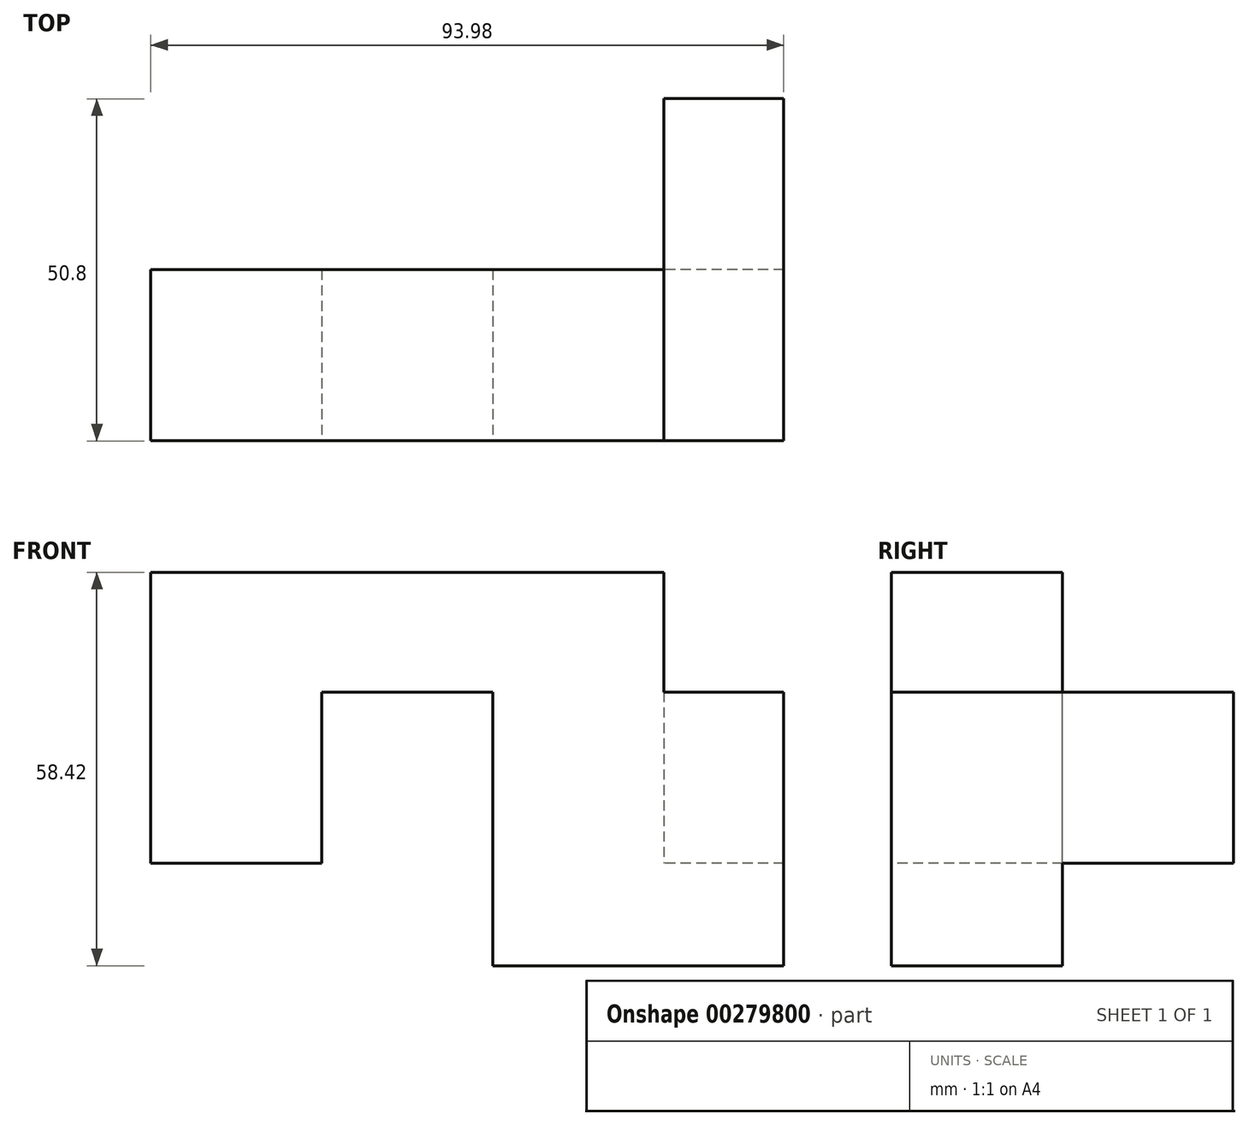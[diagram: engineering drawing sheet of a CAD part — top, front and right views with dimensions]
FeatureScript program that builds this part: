
annotation { "Feature Type Name" : "Feature", "Feature Type Description" : "" }
export const myFeature = defineFeature(function(context is Context, id is Id, definition is map)
    precondition{}
    {
        {
            var Q0;
            Q0=qCreatedBy(makeId("Right.planeOp"),FACE);
            var sketch = newSketch(context, id + "F0", { "sketchPlane" : qUnion([Q0])});
            skLineSegment(sketch, "E0.bottom", {"start": v(27.06, 34.15) * mm, "end": v(52.46, 34.15) * mm});
            skLineSegment(sketch, "E0.top", {"start": v(27.06, 8.75) * mm, "end": v(52.46, 8.75) * mm});
            skLineSegment(sketch, "E0.left", {"start": v(27.06, 34.15) * mm, "end": v(27.06, 8.75) * mm});
            skLineSegment(sketch, "E0.right", {"start": v(52.46, 34.15) * mm, "end": v(52.46, 8.75) * mm});
            skSolve(sketch);
        }
        {
            var Q0;
            Q0=makeQuery(id+"F0.imprint","IMPRINT",FACE,{"disambiguationData":[TD([[makeQuery(id+"F0.imprint","IMPRINT",EDGE,{"derivedFrom":sQuery(id+"F0.wireOp",EDGE,"E0.bottom")}),-1.0]])]});
            extrude(context, id + "F1", {"entities" : qUnion([Q0]), "depth" : 17.78 * mm});
        }
        {
            var Q0;
            Q0=makeQuery(id+"F1.opExtrude","SWEPT_FACE",FACE,{"disambiguationData":[OSD([sQuery(id+"F0.wireOp",EDGE,"E0.left")])]});
            extrude(context, id + "F2", {"entities" : qUnion([Q0]), "operationType" : NewBodyOperationType.ADD, "depth" : 25.4 * mm});
        }
        {
            var Q0;
            {var subQ0=sQuery(id+"F0.wireOp",EDGE,"E0.top");Q0=makeQuery(id+"F2.boolean.opBoolean","MERGE",FACE,{"derivedFrom":[makeQuery(id+"F1.opExtrude","SWEPT_FACE",FACE,{"disambiguationData":[OSD([subQ0])]}),makeQuery(id+"F2.opExtrude","SWEPT_FACE",FACE,{"disambiguationData":[OSD([subQ0,sQuery(id+"F0.wireOp",EDGE,"E0.left")])]})]});}
            var sketch = newSketch(context, id + "F3", { "sketchPlane" : qUnion([Q0])});
            skLineSegment(sketch, "E1", {"start": v(17.78, -27.06) * mm, "end": v(0, -27.06) * mm});
            skSolve(sketch);
        }
        {
            var Q0;
            {var subQ0=sQuery(id+"F3.wireOp",EDGE,"E1");Q0=makeQuery(id+"F3.imprint","IMPRINT",FACE,{"disambiguationData":[TD([[makeQuery(id+"F3.imprint","IMPRINT",EDGE,{"derivedFrom":subQ0}),-1.0]])]});}
            extrude(context, id + "F4", {"entities" : qUnion([Q0]), "operationType" : NewBodyOperationType.ADD, "depth" : 15.24 * mm});
        }
        {
            var Q0;
            {var subQ0=sQuery(id+"F0.wireOp",EDGE,"E0.left");var subQ1=sQuery(id+"F0.wireOp",EDGE,"E0.top");var subQ2=makeQuery(id+"F2.boolean.opBoolean","MERGE",EDGE,{"derivedFrom":[makeQuery(id+"F1.opExtrude","CAP_EDGE",EDGE,{"disambiguationData":[OSD([subQ1])],"isStart":true}),makeQuery(id+"F2.opExtrude","SWEPT_EDGE",EDGE,{"disambiguationData":[OSD([subQ1,subQ0]),TDD([makeQuery(id+"F1.opExtrude","CAP_VERTEX",VERTEX,{"disambiguationData":[OSD([subQ1,subQ0])],"isStart":true})])]})]});Q0=makeQuery(id+"F4.boolean.opBoolean","MERGE",FACE,{"derivedFrom":[makeQuery(id+"F2.boolean.opBoolean","MERGE",FACE,{"derivedFrom":[makeQuery(id+"F1.opExtrude","CAP_FACE",FACE,{"disambiguationData":[OSD([sQuery(id+"F0.wireOp",EDGE,"E0.bottom"),subQ1,subQ0,sQuery(id+"F0.wireOp",EDGE,"E0.right")])],"isStart":true}),makeQuery(id+"F2.opExtrude","SWEPT_FACE",FACE,{"disambiguationData":[OSD([subQ0]),TDD([makeQuery(id+"F1.opExtrude","CAP_EDGE",EDGE,{"disambiguationData":[OSD([subQ0])],"isStart":true})])]})]}),makeQuery(id+"F4.opExtrude","SWEPT_FACE",FACE,{"disambiguationData":[OSD([subQ1,subQ0]),TDD([makeQuery(id+"F3.imprint","IMPRINT",EDGE,{"disambiguationData":[TD([[makeQuery(id+"F3.imprint","INTERSECT",VERTEX,{"derivedFrom":[subQ2,sQuery(id+"F3.wireOp",EDGE,"E1")]}),1.0]])],"derivedFrom":subQ2})])]})]});}
            var sketch = newSketch(context, id + "F5", { "sketchPlane" : qUnion([Q0])});
            skLineSegment(sketch, "E2", {"start": v(-27.06, 8.75) * mm, "end": v(-27.06, 34.15) * mm});
            skSolve(sketch);
        }
        {
            var Q0;
            {var subQ7=sQuery(id+"F5.wireOp",EDGE,"E2");Q0=makeQuery(id+"F5.imprint","IMPRINT",FACE,{"disambiguationData":[TD([[makeQuery(id+"F5.imprint","IMPRINT",EDGE,{"derivedFrom":subQ7}),-1.0]])]});}
            extrude(context, id + "F6", {"entities" : qUnion([Q0]), "operationType" : NewBodyOperationType.ADD, "depth" : 25.4 * mm});
        }
        {
            var Q0;
            {var subQ0=sQuery(id+"F0.wireOp",EDGE,"E0.left");var subQ1=sQuery(id+"F0.wireOp",EDGE,"E0.bottom");Q0=makeQuery(id+"F6.boolean.opBoolean","MERGE",FACE,{"derivedFrom":[makeQuery(id+"F2.boolean.opBoolean","MERGE",FACE,{"derivedFrom":[makeQuery(id+"F1.opExtrude","SWEPT_FACE",FACE,{"disambiguationData":[OSD([subQ1])]}),makeQuery(id+"F2.opExtrude","SWEPT_FACE",FACE,{"disambiguationData":[OSD([subQ1,subQ0])]})]}),makeQuery(id+"F6.opExtrude","SWEPT_FACE",FACE,{"disambiguationData":[OSD([subQ1,subQ0])]})]});}
            var sketch = newSketch(context, id + "F7", { "sketchPlane" : qUnion([Q0])});
            skLineSegment(sketch, "E3", {"start": v(0, 27.06) * mm, "end": v(0, 1.66) * mm});
            skSolve(sketch);
        }
        {
            var Q0;
            {var subQ0=sQuery(id+"F7.wireOp",EDGE,"E3");Q0=makeQuery(id+"F7.imprint","IMPRINT",FACE,{"disambiguationData":[TD([[makeQuery(id+"F7.imprint","IMPRINT",EDGE,{"derivedFrom":subQ0}),-1.0]])]});}
            extrude(context, id + "F8", {"entities" : qUnion([Q0]), "operationType" : NewBodyOperationType.ADD, "depth" : 17.78 * mm});
        }
        {
            var Q0;
            {var subQ0=sQuery(id+"F0.wireOp",EDGE,"E0.left");var subQ1=sQuery(id+"F0.wireOp",EDGE,"E0.bottom");Q0=makeQuery(id+"F8.boolean.opBoolean","MERGE",FACE,{"derivedFrom":[makeQuery(id+"F6.opExtrude","CAP_FACE",FACE,{"disambiguationData":[OSD([subQ1,sQuery(id+"F0.wireOp",EDGE,"E0.top"),subQ0,sQuery(id+"F3.wireOp",EDGE,"E1"),sQuery(id+"F5.wireOp",EDGE,"E2")])],"isStart":false}),makeQuery(id+"F8.opExtrude","SWEPT_FACE",FACE,{"disambiguationData":[OSD([subQ1,subQ0])]})]});}
            var sketch = newSketch(context, id + "F9", { "sketchPlane" : qUnion([Q0])});
            skLineSegment(sketch, "E4", {"start": v(-27.06, 34.15) * mm, "end": v(-1.66, 34.15) * mm});
            skSolve(sketch);
        }
        {
            var Q0;
            {var subQ0=sQuery(id+"F9.wireOp",EDGE,"E4");Q0=makeQuery(id+"F9.imprint","IMPRINT",FACE,{"disambiguationData":[TD([[makeQuery(id+"F9.imprint","IMPRINT",EDGE,{"derivedFrom":subQ0}),1.0]])]});}
            extrude(context, id + "F10", {"entities" : qUnion([Q0]), "operationType" : NewBodyOperationType.ADD, "depth" : 50.8 * mm});
        }
        {
            var Q0;
            Q0=makeQuery(id+"F10.opExtrude","SWEPT_FACE",FACE,{"disambiguationData":[OSD([sQuery(id+"F9.wireOp",EDGE,"E4")])]});
            var sketch = newSketch(context, id + "F11", { "sketchPlane" : qUnion([Q0])});
            skLineSegment(sketch, "E5", {"start": v(-50.8, -27.06) * mm, "end": v(-50.8, -1.66) * mm});
            skSolve(sketch);
        }
        {
            var Q0;
            {var subQ0=sQuery(id+"F11.wireOp",EDGE,"E5");Q0=makeQuery(id+"F11.imprint","IMPRINT",FACE,{"disambiguationData":[TD([[makeQuery(id+"F11.imprint","IMPRINT",EDGE,{"derivedFrom":subQ0}),1.0]])]});}
            extrude(context, id + "F12", {"entities" : qUnion([Q0]), "operationType" : NewBodyOperationType.ADD, "depth" : 25.4 * mm});
        }
    });
